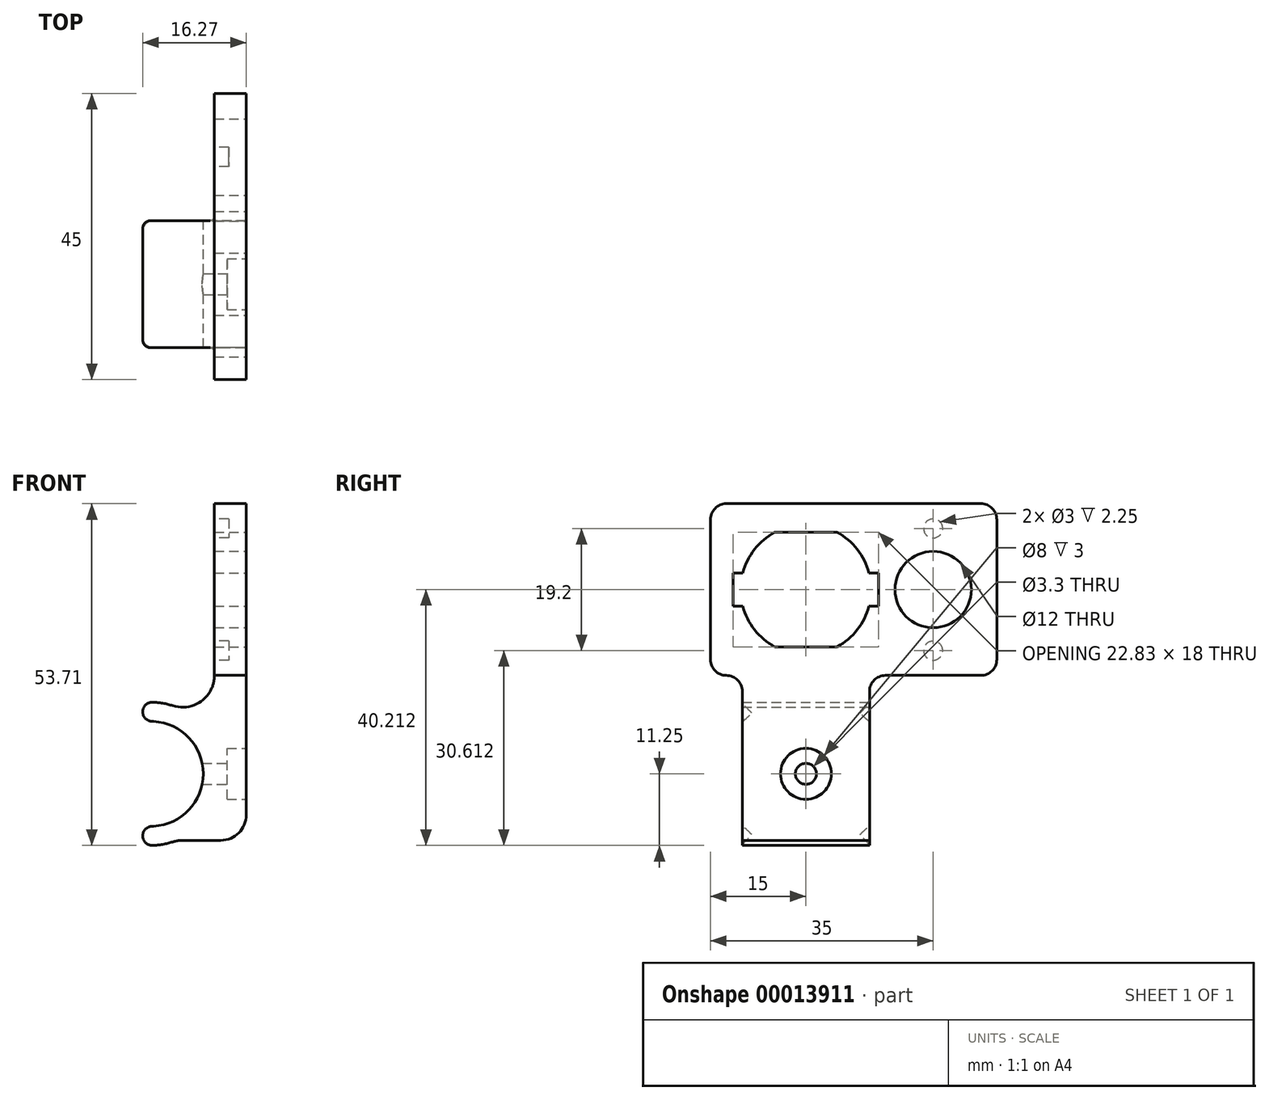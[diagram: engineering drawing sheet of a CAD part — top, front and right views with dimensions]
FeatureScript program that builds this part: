
annotation { "Feature Type Name" : "Feature", "Feature Type Description" : "" }
export const myFeature = defineFeature(function(context is Context, id is Id, definition is map)
    precondition{}
    {
        {
            var Q0;
            Q0=qCreatedBy(makeId("Front.planeOp"),FACE);
            var sketch = newSketch(context, id + "F0", { "sketchPlane" : qUnion([Q0])});
            skArc(sketch, "E0", {"start": v(-1.08, -8.18) * mm, "mid": v(8.25, 0) * mm, "end": v(-1.08, 8.18) * mm});
            skArc(sketch, "E1", {"start": v(3.46, 10.7) * mm, "mid": v(1.02, 11.2) * mm, "end": v(-1.47, 11.15) * mm});
            skLineSegment(sketch, "E2", {"start": v(-1.08, 8.18) * mm, "end": v(-1.47, 11.15) * mm});
            skLineSegment(sketch, "E3", {"start": v(-1.08, -8.18) * mm, "end": v(-1.47, -11.15) * mm});
            skLineSegment(sketch, "E4", {"start": v(0, 0) * mm, "end": v(-11.25, 0) * mm, "construction": true});
            skLineSegment(sketch, "E5", {"start": v(10, 15.46) * mm, "end": v(10, 42.46) * mm});
            skLineSegment(sketch, "E6", {"start": v(15, 0) * mm, "end": v(15, 42.46) * mm});
            skPoint(sketch, "E7.orphan", {"position": v(8.25, 0) * mm});
            skArc(sketch, "E8.trimOffspring", {"start": v(-1.47, -11.15) * mm, "mid": v(1.02, -11.2) * mm, "end": v(3.46, -10.7) * mm});
            skPoint(sketch, "E9.visualSharp", {"position": v(8.18, 7.72) * mm});
            skArc(sketch, "E9.filletArc", {"start": v(3.46, 10.7) * mm, "mid": v(7.94, 11.42) * mm, "end": v(10, 15.46) * mm});
            skLineSegment(sketch, "E10.MirrorCS", {"start": v(15, 0) * mm, "end": v(15, -6.46) * mm});
            skArc(sketch, "E11.MirrorCS", {"start": v(3.46, -10.7) * mm, "mid": v(4.22, -10.52) * mm, "end": v(5, -10.46) * mm});
            skLineSegment(sketch, "E12", {"start": v(5, -10.46) * mm, "end": v(11, -10.46) * mm});
            skPoint(sketch, "E13.visualSharp", {"position": v(15, -10.46) * mm});
            skArc(sketch, "E13.filletArc", {"start": v(11, -10.46) * mm, "mid": v(13.83, -9.3) * mm, "end": v(15, -6.46) * mm});
            skLineSegment(sketch, "E14", {"start": v(10, 42.46) * mm, "end": v(15, 42.46) * mm});
            skSolve(sketch);
        }
        {
            var Q0;
            Q0 = qSketchRegion(id + "F0", true);
            extrude(context, id + "F1", {"entities" : qUnion([Q0]), "depth" : 10 * mm, "hasSecondDirection" : true, "secondDirectionOppositeDirection" : true, "secondDirectionDepth" : 10 * mm});
        }
        {
            var Q0;
            Q0=makeQuery(id+"F1.opExtrude","SWEPT_FACE",FACE,{"disambiguationData":[OSD([sQuery(id+"F0.wireOp",EDGE,"E6"),sQuery(id+"F0.wireOp",EDGE,"E10.MirrorCS")])]});
            var sketch = newSketch(context, id + "F2", { "sketchPlane" : qUnion([Q0])});
            skCircle(sketch, "E15", {"center": v(0, 0) * mm, "radius": 4 * mm});
            skSolve(sketch);
        }
        {
            var Q0;
            Q0 = qSketchRegion(id + "F2", true);
            extrude(context, id + "F3", {"entities" : qUnion([Q0]), "operationType" : NewBodyOperationType.REMOVE, "oppositeDirection" : true, "depth" : 3 * mm});
        }
        {
            var Q0;
            Q0=makeQuery(id+"F3.boolean.opBoolean","COPY",FACE,{"derivedFrom":makeQuery(id+"F3.opExtrude","CAP_FACE",FACE,{"disambiguationData":[OSD([sQuery(id+"F2.wireOp",EDGE,"E15")])],"isStart":false})});
            var sketch = newSketch(context, id + "F4", { "sketchPlane" : qUnion([Q0])});
            skCircle(sketch, "E16", {"center": v(0, 0) * mm, "radius": 1.65 * mm});
            skSolve(sketch);
        }
        {
            var Q0;
            Q0 = qSketchRegion(id + "F4", true);
            extrude(context, id + "F5", {"entities" : qUnion([Q0]), "operationType" : NewBodyOperationType.REMOVE, "endBound" : BoundingType.UP_TO_NEXT, "oppositeDirection" : true, "depth" : 25 * mm});
        }
        {
            var Q0;
            Q0=makeQuery(id+"F1.opExtrude","SWEPT_FACE",FACE,{"disambiguationData":[OSD([sQuery(id+"F0.wireOp",EDGE,"E3")])]});
            var Q1;
            Q1=makeQuery(id+"F1.opExtrude","SWEPT_FACE",FACE,{"disambiguationData":[OSD([sQuery(id+"F0.wireOp",EDGE,"E2")])]});
            var Q2;
            Q2=makeQuery(id+"FjnuNmXrtYn348j_1.opExtrude","SWEPT_FACE",FACE,{"disambiguationData":[OSD([sQuery(id+"Fa3RWZgoeF39FN2_1.wireOp",EDGE,"51898195-168c-4ef9-889b-3f25a61ebd54.right")])]});
            var Q3;
            Q3=makeQuery(id+"F1.opExtrude","SWEPT_FACE",FACE,{"disambiguationData":[OSD([sQuery(id+"F0.wireOp",EDGE,"c80ee802-327a-40aa-a437-39265bece705")])]});
            var Q4;
            Q4=makeQuery(id+"F1.opExtrude","SWEPT_FACE",FACE,{"disambiguationData":[OSD([sQuery(id+"F0.wireOp",EDGE,"27b64a80-8438-4588-bf8c-cdaa58da40bb1.MirrorCS")])]});
            var Q5;
            Q5=makeQuery(id+"F1.opExtrude","SWEPT_FACE",FACE,{"disambiguationData":[OSD([sQuery(id+"F0.wireOp",EDGE,"3212bea0-b15d-4d11-89e9-7901f5facefd")])]});
            var Q6;
            Q6=makeQuery(id+"F1.opExtrude","SWEPT_FACE",FACE,{"disambiguationData":[OSD([sQuery(id+"F0.wireOp",EDGE,"526ff41d-5b7c-49a9-9487-4c90a5792b852.MirrorCS")])]});
            fillet(context, id + "F6", {"entities" : qUnion([Q0, Q1, Q2, Q3, Q4, Q5, Q6]), "radius" : 1.5 * mm, "tangentPropagation" : true, "allowEdgeOverflow" : false});
        }
        {
            var Q0;
            Q0=qCreatedBy(makeId("Front.planeOp"),FACE);
            var sketch = newSketch(context, id + "F7", { "sketchPlane" : qUnion([Q0])});
            skLineSegment(sketch, "E17.0", {"start": v(10, 15.46) * mm, "end": v(10, 42.46) * mm});
            skLineSegment(sketch, "E17.1", {"start": v(10, 42.46) * mm, "end": v(15, 42.46) * mm});
            skLineSegment(sketch, "E17.2", {"start": v(15, 42.46) * mm, "end": v(15, 15.46) * mm});
            skLineSegment(sketch, "E18", {"start": v(10, 15.46) * mm, "end": v(15, 15.46) * mm});
            skSolve(sketch);
        }
        {
            var Q0;
            Q0 = qSketchRegion(id + "F7", true);
            extrude(context, id + "F8", {"entities" : qUnion([Q0]), "operationType" : NewBodyOperationType.ADD, "depth" : 15 * mm, "hasSecondDirection" : true, "secondDirectionOppositeDirection" : true, "secondDirectionDepth" : 30 * mm});
        }
        {
            var Q0;
            Q0=makeQuery(id+"F8.boolean.opBoolean","INTERSECT",EDGE,{"derivedFrom":[makeQuery(id+"F1.opExtrude","CAP_FACE",FACE,{"disambiguationData":[OSD([sQuery(id+"F0.wireOp",EDGE,"E0"),sQuery(id+"F0.wireOp",EDGE,"E1"),sQuery(id+"F0.wireOp",EDGE,"E2"),sQuery(id+"F0.wireOp",EDGE,"E3"),sQuery(id+"F0.wireOp",EDGE,"E5"),sQuery(id+"F0.wireOp",EDGE,"E6"),sQuery(id+"F0.wireOp",EDGE,"E8.trimOffspring"),sQuery(id+"F0.wireOp",EDGE,"E9.filletArc"),sQuery(id+"F0.wireOp",EDGE,"E10.MirrorCS"),sQuery(id+"F0.wireOp",EDGE,"E11.MirrorCS"),sQuery(id+"F0.wireOp",EDGE,"E12"),sQuery(id+"F0.wireOp",EDGE,"E13.filletArc"),sQuery(id+"F0.wireOp",EDGE,"E14")])],"isStart":false}),makeQuery(id+"F8.opExtrude","SWEPT_FACE",FACE,{"disambiguationData":[OSD([sQuery(id+"F7.wireOp",EDGE,"E18")])]})]});
            var Q1;
            Q1=makeQuery(id+"F8.opExtrude","CAP_EDGE",EDGE,{"disambiguationData":[OSD([sQuery(id+"F7.wireOp",EDGE,"E18")])],"isStart":false});
            var Q2;
            Q2=makeQuery(id+"F8.boolean.opBoolean","INTERSECT",EDGE,{"derivedFrom":[makeQuery(id+"F1.opExtrude","CAP_FACE",FACE,{"disambiguationData":[OSD([sQuery(id+"F0.wireOp",EDGE,"E0"),sQuery(id+"F0.wireOp",EDGE,"E1"),sQuery(id+"F0.wireOp",EDGE,"E2"),sQuery(id+"F0.wireOp",EDGE,"E3"),sQuery(id+"F0.wireOp",EDGE,"E5"),sQuery(id+"F0.wireOp",EDGE,"E6"),sQuery(id+"F0.wireOp",EDGE,"E8.trimOffspring"),sQuery(id+"F0.wireOp",EDGE,"E9.filletArc"),sQuery(id+"F0.wireOp",EDGE,"E10.MirrorCS"),sQuery(id+"F0.wireOp",EDGE,"E11.MirrorCS"),sQuery(id+"F0.wireOp",EDGE,"E12"),sQuery(id+"F0.wireOp",EDGE,"E13.filletArc"),sQuery(id+"F0.wireOp",EDGE,"E14")])],"isStart":true}),makeQuery(id+"F8.opExtrude","SWEPT_FACE",FACE,{"disambiguationData":[OSD([sQuery(id+"F7.wireOp",EDGE,"E18")])]})]});
            var Q3;
            Q3=makeQuery(id+"F8.opExtrude","CAP_EDGE",EDGE,{"disambiguationData":[OSD([sQuery(id+"F7.wireOp",EDGE,"E18")])],"isStart":true});
            var Q4;
            Q4=makeQuery(id+"F8.opExtrude","CAP_EDGE",EDGE,{"disambiguationData":[OSD([sQuery(id+"F7.wireOp",EDGE,"E17.1")])],"isStart":true});
            var Q5;
            Q5=makeQuery(id+"F8.opExtrude","CAP_EDGE",EDGE,{"disambiguationData":[OSD([sQuery(id+"F7.wireOp",EDGE,"E17.1")])],"isStart":false});
            fillet(context, id + "F9", {"entities" : qUnion([Q0, Q1, Q2, Q3, Q4, Q5]), "radius" : 2.5 * mm, "tangentPropagation" : true, "allowEdgeOverflow" : false});
        }
        {
            var Q0;
            Q0=makeQuery(id+"F8.boolean.opBoolean","MERGE",FACE,{"derivedFrom":[makeQuery(id+"F1.opExtrude","SWEPT_FACE",FACE,{"disambiguationData":[OSD([sQuery(id+"F0.wireOp",EDGE,"E6"),sQuery(id+"F0.wireOp",EDGE,"E10.MirrorCS")])]}),makeQuery(id+"F8.opExtrude","SWEPT_FACE",FACE,{"disambiguationData":[OSD([sQuery(id+"F7.wireOp",EDGE,"E17.2")])]})]});
            var sketch = newSketch(context, id + "F10", { "sketchPlane" : qUnion([Q0])});
            skArc(sketch, "E19", {"start": v(-9.91, 26.36) * mm, "mid": v(-8.07, 22.64) * mm, "end": v(-4.9, 19.96) * mm});
            skLineSegment(sketch, "E20", {"start": v(0, 28.96) * mm, "end": v(30, 28.96) * mm, "construction": true});
            skLineSegment(sketch, "E21", {"start": v(-4.9, 19.96) * mm, "end": v(4.9, 19.96) * mm});
            skLineSegment(sketch, "E22", {"start": v(4.9, 37.96) * mm, "end": v(-4.9, 37.96) * mm});
            skLineSegment(sketch, "E23.bottom", {"start": v(9.91, 31.56) * mm, "end": v(11.41, 31.56) * mm});
            skLineSegment(sketch, "E23.top", {"start": v(9.91, 26.36) * mm, "end": v(11.41, 26.36) * mm});
            skLineSegment(sketch, "E23.right", {"start": v(11.41, 31.56) * mm, "end": v(11.41, 26.36) * mm});
            skLineSegment(sketch, "E24", {"start": v(0, 28.96) * mm, "end": v(0, 43.64) * mm, "construction": true});
            skLineSegment(sketch, "E25.MirrorCS", {"start": v(-9.91, 31.56) * mm, "end": v(-11.41, 31.56) * mm});
            skLineSegment(sketch, "E26.MirrorCS", {"start": v(-11.41, 31.56) * mm, "end": v(-11.41, 26.36) * mm});
            skLineSegment(sketch, "E27.MirrorCS", {"start": v(-9.91, 26.36) * mm, "end": v(-11.41, 26.36) * mm});
            skArc(sketch, "E28.trimOffspring", {"start": v(9.91, 31.56) * mm, "mid": v(8.07, 35.28) * mm, "end": v(4.9, 37.96) * mm});
            skArc(sketch, "E29.trimOffspring", {"start": v(4.9, 19.96) * mm, "mid": v(8.07, 22.64) * mm, "end": v(9.91, 26.36) * mm});
            skArc(sketch, "E30.trimOffspring", {"start": v(-4.9, 37.96) * mm, "mid": v(-8.07, 35.28) * mm, "end": v(-9.91, 31.56) * mm});
            skSolve(sketch);
        }
        {
            var Q0;
            Q0 = qSketchRegion(id + "F10", true);
            extrude(context, id + "F11", {"entities" : qUnion([Q0]), "operationType" : NewBodyOperationType.REMOVE, "endBound" : BoundingType.UP_TO_NEXT, "oppositeDirection" : true, "depth" : 25 * mm});
        }
        {
            var Q0;
            Q0=makeQuery(id+"F8.boolean.opBoolean","MERGE",FACE,{"derivedFrom":[makeQuery(id+"F1.opExtrude","SWEPT_FACE",FACE,{"disambiguationData":[OSD([sQuery(id+"F0.wireOp",EDGE,"E6"),sQuery(id+"F0.wireOp",EDGE,"E10.MirrorCS")])]}),makeQuery(id+"F8.opExtrude","SWEPT_FACE",FACE,{"disambiguationData":[OSD([sQuery(id+"F7.wireOp",EDGE,"E17.2")])]})]});
            var sketch = newSketch(context, id + "F12", { "sketchPlane" : qUnion([Q0])});
            skCircle(sketch, "E31", {"center": v(20, 28.96) * mm, "radius": 6 * mm});
            skLineSegment(sketch, "E32", {"start": v(20, 28.96) * mm, "end": v(0, 28.96) * mm, "construction": true});
            skSolve(sketch);
        }
        {
            var Q0;
            Q0 = qSketchRegion(id + "F12", true);
            extrude(context, id + "F13", {"entities" : qUnion([Q0]), "operationType" : NewBodyOperationType.REMOVE, "endBound" : BoundingType.UP_TO_NEXT, "oppositeDirection" : true, "depth" : 25 * mm});
        }
        {
            var Q0;
            Q0=makeQuery(id+"F8.boolean.opBoolean","MERGE",FACE,{"derivedFrom":[makeQuery(id+"F1.opExtrude","SWEPT_FACE",FACE,{"disambiguationData":[OSD([sQuery(id+"F0.wireOp",EDGE,"E5")])]}),makeQuery(id+"F8.opExtrude","SWEPT_FACE",FACE,{"disambiguationData":[OSD([sQuery(id+"F7.wireOp",EDGE,"E17.0")])]})]});
            var sketch = newSketch(context, id + "F14", { "sketchPlane" : qUnion([Q0])});
            skLineSegment(sketch, "E33", {"start": v(-20, 28.96) * mm, "end": v(0, 28.96) * mm, "construction": true});
            skLineSegment(sketch, "E34", {"start": v(-20, 38.56) * mm, "end": v(-20, 19.36) * mm, "construction": true});
            skCircle(sketch, "E35", {"center": v(-20, 38.56) * mm, "radius": 1.5 * mm});
            skCircle(sketch, "E36", {"center": v(-20, 19.36) * mm, "radius": 1.5 * mm});
            skSolve(sketch);
        }
        {
            var Q0;
            Q0 = qSketchRegion(id + "F14", true);
            extrude(context, id + "F15", {"entities" : qUnion([Q0]), "operationType" : NewBodyOperationType.REMOVE, "oppositeDirection" : true, "depth" : 2.25 * mm});
        }
    });
